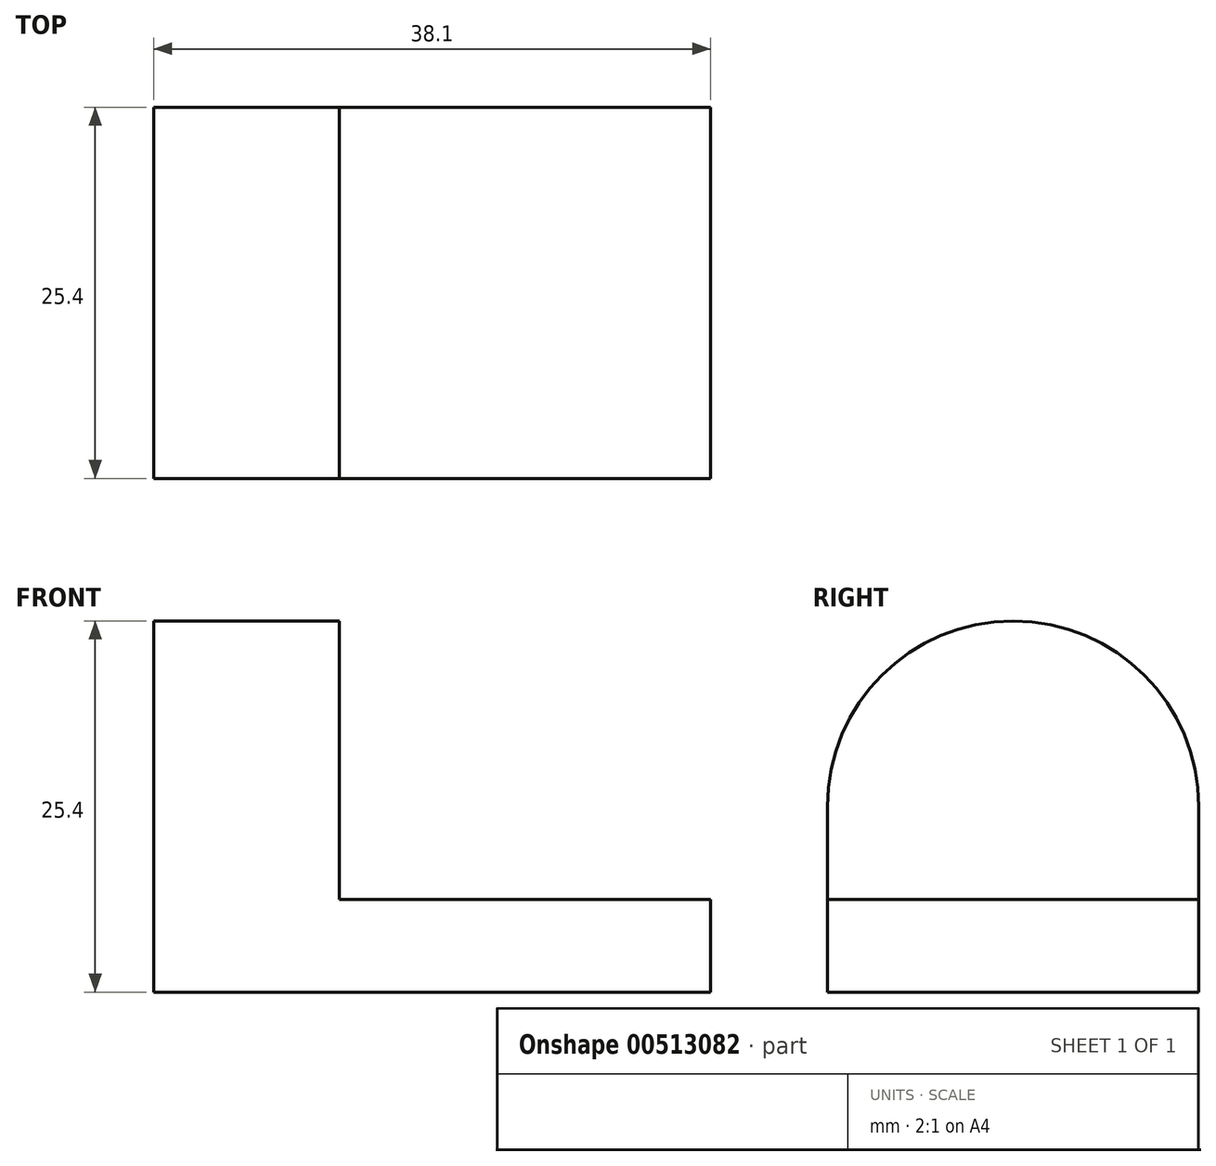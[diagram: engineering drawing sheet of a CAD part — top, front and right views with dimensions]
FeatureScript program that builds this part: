
annotation { "Feature Type Name" : "Feature", "Feature Type Description" : "" }
export const myFeature = defineFeature(function(context is Context, id is Id, definition is map)
    precondition{}
    {
        {
            var Q0;
            Q0=qCreatedBy(makeId("Right.planeOp"),FACE);
            var sketch = newSketch(context, id + "F0", { "sketchPlane" : qUnion([Q0])});
            skLineSegment(sketch, "E0", {"start": v(0, 0) * mm, "end": v(0, 12.7) * mm});
            skLineSegment(sketch, "E1", {"start": v(0, 0) * mm, "end": v(25.4, 0) * mm});
            skLineSegment(sketch, "E2", {"start": v(25.4, 0) * mm, "end": v(25.4, 12.7) * mm});
            skArc(sketch, "E3", {"start": v(25.4, 12.7) * mm, "mid": v(12.7, 25.4) * mm, "end": v(0, 12.7) * mm});
            skSolve(sketch);
        }
        {
            var Q0;
            Q0=makeQuery(id+"F0.imprint","IMPRINT",FACE,{"disambiguationData":[TD([[makeQuery(id+"F0.imprint","IMPRINT",EDGE,{"derivedFrom":sQuery(id+"F0.wireOp",EDGE,"E0")}),-1.0]])]});
            extrude(context, id + "F1", {"entities" : qUnion([Q0]), "depth" : 12.7 * mm});
        }
        {
            var Q0;
            Q0=qCreatedBy(makeId("Front.planeOp"),FACE);
            var sketch = newSketch(context, id + "F2", { "sketchPlane" : qUnion([Q0])});
            skLineSegment(sketch, "E4.bottom", {"start": v(0, 0) * mm, "end": v(38.1, 0) * mm});
            skLineSegment(sketch, "E4.top", {"start": v(0, 6.35) * mm, "end": v(38.1, 6.35) * mm});
            skLineSegment(sketch, "E4.left", {"start": v(0, 0) * mm, "end": v(0, 6.35) * mm});
            skLineSegment(sketch, "E4.right", {"start": v(38.1, 0) * mm, "end": v(38.1, 6.35) * mm});
            skSolve(sketch);
        }
        {
            var Q0;
            Q0=qSketchRegion(id+"F2",true);
            extrude(context, id + "F3", {"entities" : qUnion([Q0]), "operationType" : NewBodyOperationType.ADD, "oppositeDirection" : true, "depth" : 25.4 * mm});
        }
    });
